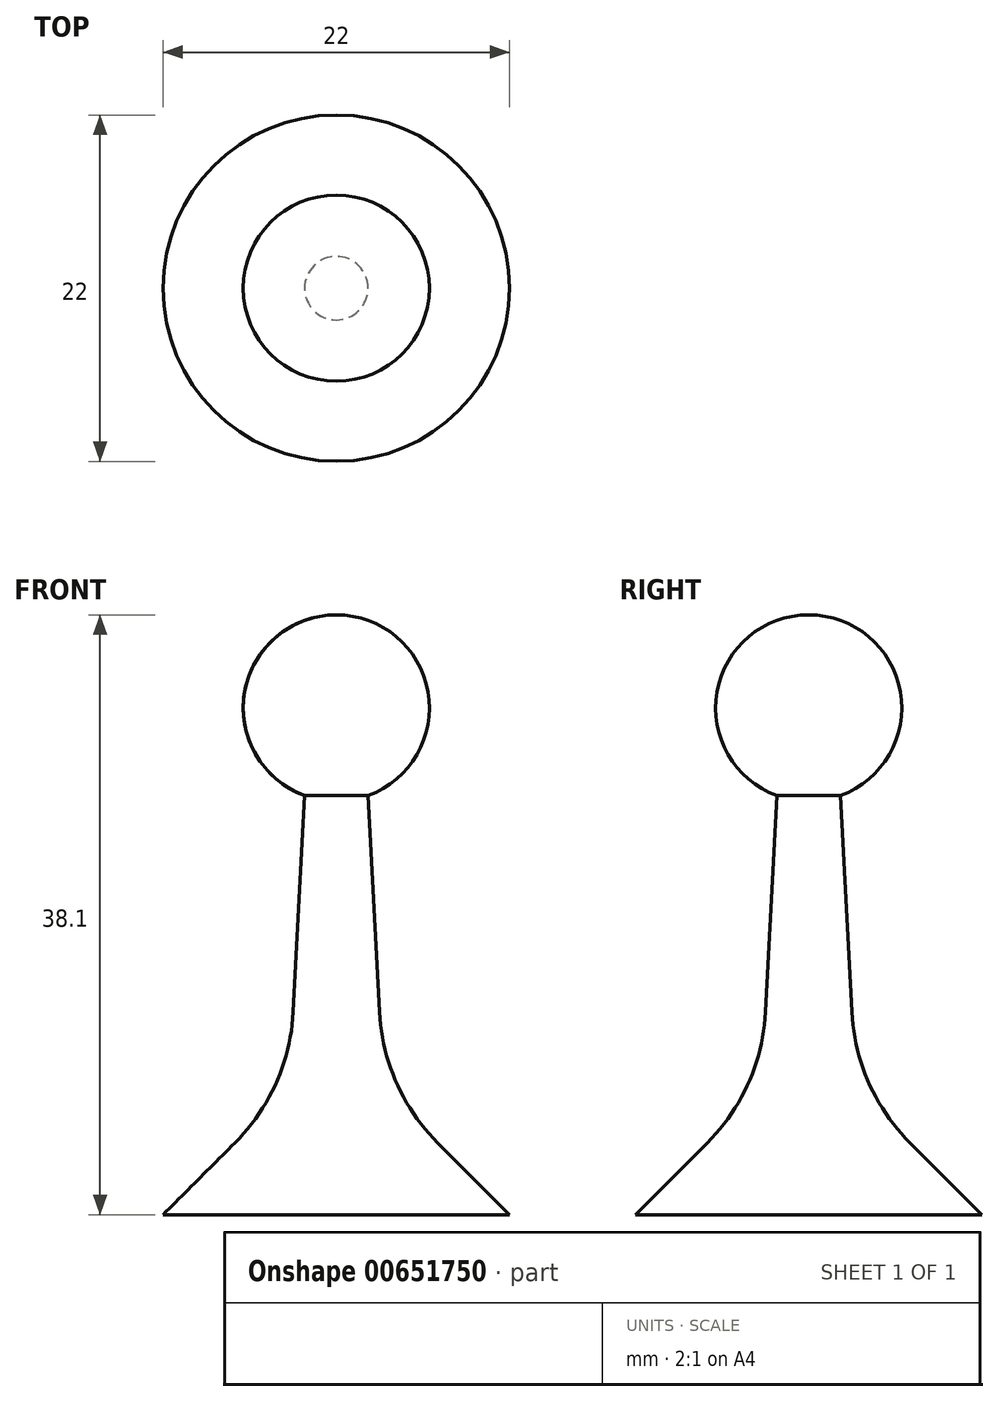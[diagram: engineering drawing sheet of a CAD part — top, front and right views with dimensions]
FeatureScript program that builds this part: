
annotation { "Feature Type Name" : "Feature", "Feature Type Description" : "" }
export const myFeature = defineFeature(function(context is Context, id is Id, definition is map)
    precondition{}
    {
        {
            var Q0;
            Q0=qCreatedBy(makeId("Front.planeOp"),FACE);
            var sketch = newSketch(context, id + "F0", { "sketchPlane" : qUnion([Q0])});
            skLineSegment(sketch, "E0", {"start": v(-11, 0) * mm, "end": v(0, 0) * mm});
            skLineSegment(sketch, "E1", {"start": v(0, 0) * mm, "end": v(0, 38.1) * mm});
            skLineSegment(sketch, "E2", {"start": v(-11, 0) * mm, "end": v(-6.44, 4.56) * mm});
            skLineSegment(sketch, "E3", {"start": v(-2.74, 12.87) * mm, "end": v(-2.02, 26.63) * mm});
            skArc(sketch, "E4", {"start": v(0, 38.1) * mm, "mid": v(-5.82, 33.21) * mm, "end": v(-2.02, 26.63) * mm});
            skPoint(sketch, "E5.visualSharp", {"position": v(-3, 8) * mm});
            skArc(sketch, "E5.filletArc", {"start": v(-6.44, 4.56) * mm, "mid": v(-3.82, 8.37) * mm, "end": v(-2.74, 12.87) * mm});
            skSolve(sketch);
        }
        {
            var Q0;
            Q0 = qSketchRegion(id + "F0", true);
            var Q1;
            Q1=sQuery(id+"F0.wireOp",EDGE,"E1");
            revolve(context, id + "F1", {"entities" : qUnion([Q0]), "axis" : qUnion([Q1]), "revolveType" : RevolveType.FULL});
        }
    });
